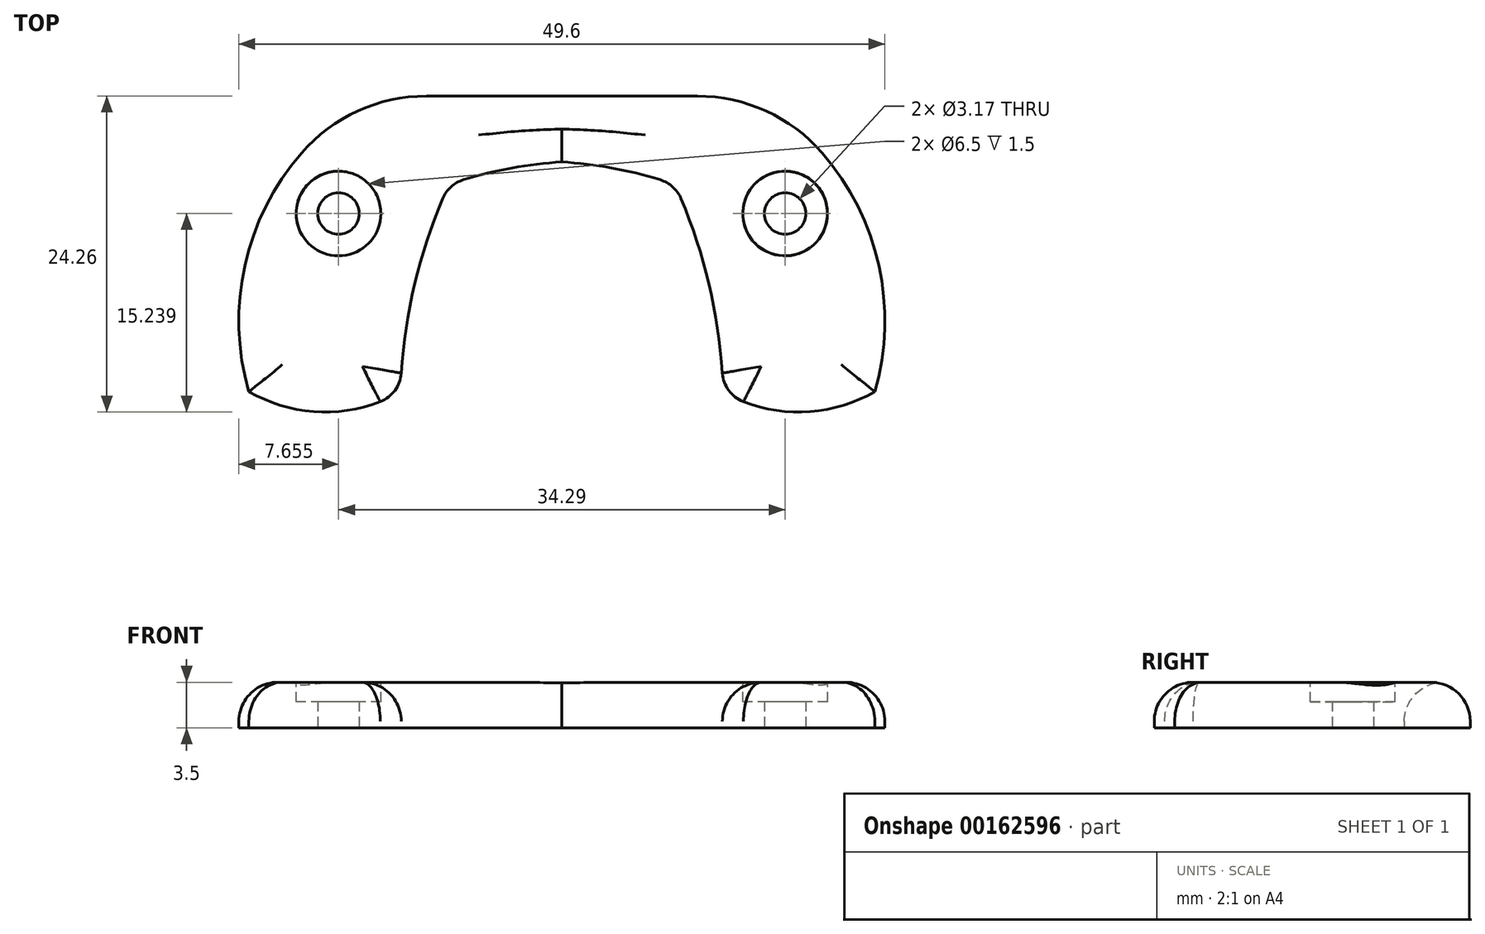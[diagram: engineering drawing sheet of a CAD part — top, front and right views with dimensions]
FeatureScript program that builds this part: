
annotation { "Feature Type Name" : "Feature", "Feature Type Description" : "" }
export const myFeature = defineFeature(function(context is Context, id is Id, definition is map)
    precondition{}
    {
        {
            var Q0;
            Q0=qCreatedBy(makeId("Top.planeOp"),FACE);
            var sketch = newSketch(context, id + "F0", { "sketchPlane" : qUnion([Q0])});
            skLineSegment(sketch, "E0", {"start": v(0, 0) * mm, "end": v(0, -24.32) * mm, "construction": true});
            skCircle(sketch, "E1", {"center": v(-17.15, -3.96) * mm, "radius": 1.59 * mm});
            skLineSegment(sketch, "E2", {"start": v(-10.4, 5.06) * mm, "end": v(0, 5.06) * mm});
            skArc(sketch, "E3", {"start": v(0, 0) * mm, "mid": v(-3.82, -0.46) * mm, "end": v(-7.56, -1.37) * mm});
            skArc(sketch, "E4", {"start": v(-9.15, -2.81) * mm, "mid": v(-11.3, -9.38) * mm, "end": v(-12.32, -16.2) * mm});
            skArc(sketch, "E5", {"start": v(-24.03, -17.63) * mm, "mid": v(-19.07, -19.17) * mm, "end": v(-13.94, -18.4) * mm});
            skArc(sketch, "E6", {"start": v(-19.99, 0.69) * mm, "mid": v(-24.34, -7.96) * mm, "end": v(-24.03, -17.63) * mm});
            skPoint(sketch, "E7.visualSharp", {"position": v(-14.55, 5.06) * mm});
            skArc(sketch, "E7.filletArc", {"start": v(-10.4, 5.06) * mm, "mid": v(-15.67, 3.91) * mm, "end": v(-19.99, 0.69) * mm});
            skPoint(sketch, "E8.visualSharp", {"position": v(-12.4, -17.67) * mm});
            skArc(sketch, "E8.filletArc", {"start": v(-13.94, -18.4) * mm, "mid": v(-12.81, -17.54) * mm, "end": v(-12.32, -16.2) * mm});
            skArc(sketch, "E9.MirrorCS", {"start": v(13.94, -18.4) * mm, "mid": v(12.81, -17.54) * mm, "end": v(12.32, -16.2) * mm});
            skArc(sketch, "E10.MirrorCS", {"start": v(10.4, 5.06) * mm, "mid": v(15.67, 3.91) * mm, "end": v(19.99, 0.69) * mm});
            skPoint(sketch, "E11.MirrorP", {"position": v(12.4, -17.67) * mm});
            skCircle(sketch, "E12.MirrorC", {"center": v(17.15, -3.96) * mm, "radius": 1.59 * mm});
            skArc(sketch, "E13.MirrorCS", {"start": v(19.99, 0.69) * mm, "mid": v(24.34, -7.96) * mm, "end": v(24.03, -17.63) * mm});
            skArc(sketch, "E14.MirrorCS", {"start": v(24.03, -17.63) * mm, "mid": v(19.07, -19.17) * mm, "end": v(13.94, -18.4) * mm});
            skPoint(sketch, "E15.MirrorP", {"position": v(14.55, 5.06) * mm});
            skArc(sketch, "E16.MirrorCS", {"start": v(0, 0) * mm, "mid": v(3.82, -0.46) * mm, "end": v(7.56, -1.37) * mm});
            skLineSegment(sketch, "E17.MirrorCS", {"start": v(10.4, 5.06) * mm, "end": v(0, 5.06) * mm});
            skArc(sketch, "E18.MirrorCS", {"start": v(9.15, -2.81) * mm, "mid": v(11.3, -9.38) * mm, "end": v(12.32, -16.2) * mm});
            skPoint(sketch, "E19.visualSharp", {"position": v(-8.68, -1.74) * mm});
            skArc(sketch, "E19.filletArc", {"start": v(-7.56, -1.37) * mm, "mid": v(-8.52, -1.91) * mm, "end": v(-9.15, -2.81) * mm});
            skPoint(sketch, "E20.visualSharp", {"position": v(8.68, -1.74) * mm});
            skArc(sketch, "E20.filletArc", {"start": v(9.15, -2.81) * mm, "mid": v(8.52, -1.91) * mm, "end": v(7.56, -1.37) * mm});
            skSolve(sketch);
        }
        {
            var Q0;
            Q0 = qSketchRegion(id + "F0", true);
            extrude(context, id + "F1", {"entities" : qUnion([Q0]), "depth" : 3.5 * mm});
        }
        {
            var Q0;
            Q0=makeQuery(id+"F1.opExtrude","CAP_FACE",FACE,{"disambiguationData":[OSD([sQuery(id+"F0.wireOp",EDGE,"E1"),sQuery(id+"F0.wireOp",EDGE,"E2"),sQuery(id+"F0.wireOp",EDGE,"E3"),sQuery(id+"F0.wireOp",EDGE,"E4"),sQuery(id+"F0.wireOp",EDGE,"E5"),sQuery(id+"F0.wireOp",EDGE,"E6"),sQuery(id+"F0.wireOp",EDGE,"E7.filletArc"),sQuery(id+"F0.wireOp",EDGE,"E8.filletArc"),sQuery(id+"F0.wireOp",EDGE,"E9.MirrorCS"),sQuery(id+"F0.wireOp",EDGE,"E10.MirrorCS"),sQuery(id+"F0.wireOp",EDGE,"E12.MirrorC"),sQuery(id+"F0.wireOp",EDGE,"E13.MirrorCS"),sQuery(id+"F0.wireOp",EDGE,"E14.MirrorCS"),sQuery(id+"F0.wireOp",EDGE,"E16.MirrorCS"),sQuery(id+"F0.wireOp",EDGE,"E17.MirrorCS"),sQuery(id+"F0.wireOp",EDGE,"E18.MirrorCS"),sQuery(id+"F0.wireOp",EDGE,"E19.filletArc"),sQuery(id+"F0.wireOp",EDGE,"E20.filletArc")])],"isStart":false});
            var sketch = newSketch(context, id + "F2", { "sketchPlane" : qUnion([Q0])});
            skCircle(sketch, "E21", {"center": v(-17.15, -3.96) * mm, "radius": 3.25 * mm});
            skCircle(sketch, "E22", {"center": v(17.15, -3.96) * mm, "radius": 3.25 * mm});
            skSolve(sketch);
        }
        {
            var Q0;
            Q0 = qSketchRegion(id + "F2", true);
            extrude(context, id + "F3", {"entities" : qUnion([Q0]), "operationType" : NewBodyOperationType.REMOVE, "oppositeDirection" : true, "depth" : 1.5 * mm});
        }
        {
            var Q0;
            Q0=makeQuery(id+"F1.opExtrude","CAP_EDGE",EDGE,{"disambiguationData":[OSD([sQuery(id+"F0.wireOp",EDGE,"E2"),sQuery(id+"F0.wireOp",EDGE,"E17.MirrorCS")])],"isStart":false});
            var Q1;
            Q1=makeQuery(id+"F1.opExtrude","CAP_EDGE",EDGE,{"disambiguationData":[OSD([sQuery(id+"F0.wireOp",EDGE,"E5")])],"isStart":false});
            var Q2;
            Q2=makeQuery(id+"F1.opExtrude","CAP_EDGE",EDGE,{"disambiguationData":[OSD([sQuery(id+"F0.wireOp",EDGE,"E14.MirrorCS")])],"isStart":false});
            var Q3;
            Q3=makeQuery(id+"F1.opExtrude","CAP_EDGE",EDGE,{"disambiguationData":[OSD([sQuery(id+"F0.wireOp",EDGE,"E13.MirrorCS")])],"isStart":false});
            fillet(context, id + "F4", {"entities" : qUnion([Q0, Q1, Q2, Q3]), "radius" : 3 * mm, "tangentPropagation" : true, "allowEdgeOverflow" : false});
        }
    });
